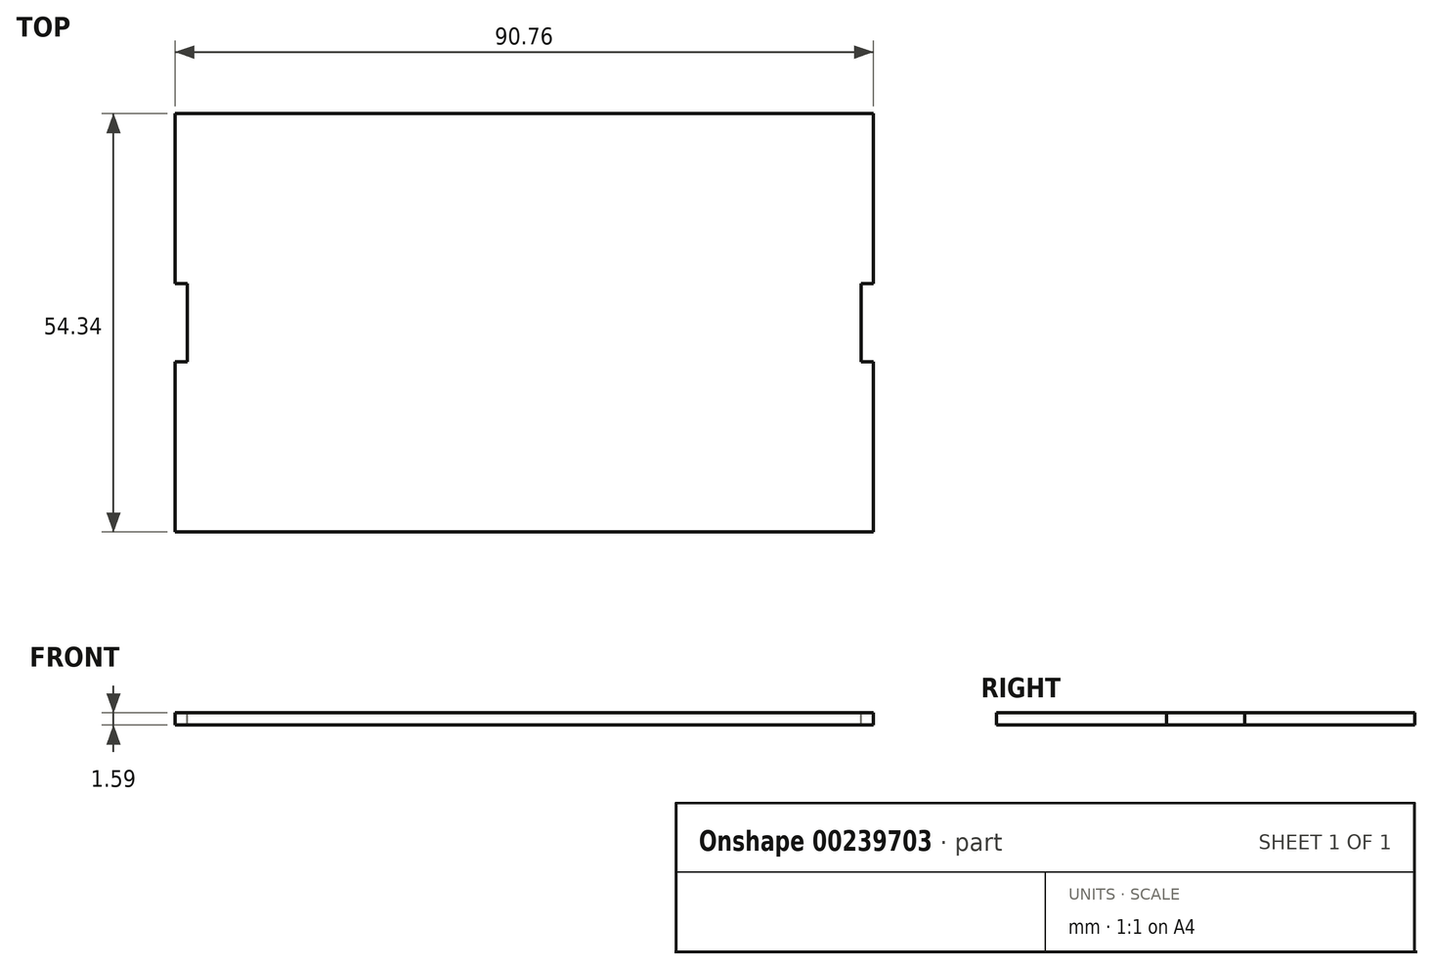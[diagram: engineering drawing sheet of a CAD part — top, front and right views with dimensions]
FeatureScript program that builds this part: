
annotation { "Feature Type Name" : "Feature", "Feature Type Description" : "" }
export const myFeature = defineFeature(function(context is Context, id is Id, definition is map)
    precondition{}
    {
        {
            var Q0;
            Q0=qCreatedBy(makeId("Top.planeOp"),FACE);
            var sketch = newSketch(context, id + "F0", { "sketchPlane" : qUnion([Q0])});
            skLineSegment(sketch, "E0.bottom", {"start": v(0, 0) * mm, "end": v(-90.76, 0) * mm});
            skLineSegment(sketch, "E0.top", {"start": v(0, 54.34) * mm, "end": v(-90.76, 54.34) * mm});
            skLineSegment(sketch, "E0.left", {"start": v(0, 0) * mm, "end": v(0, 54.34) * mm});
            skLineSegment(sketch, "E0.right", {"start": v(-90.76, 0) * mm, "end": v(-90.76, 54.34) * mm});
            skSolve(sketch);
        }
        {
            var Q0;
            Q0=makeQuery(id+"F0.imprint","IMPRINT",FACE,{"disambiguationData":[TD([[makeQuery(id+"F0.imprint","IMPRINT",EDGE,{"derivedFrom":sQuery(id+"F0.wireOp",EDGE,"E0.bottom")}),-1.0]])]});
            extrude(context, id + "F1", {"entities" : qUnion([Q0]), "depth" : 1.59 * mm});
        }
        {
            var Q0;
            Q0=makeQuery(id+"F1.opExtrude","CAP_FACE",FACE,{"disambiguationData":[OSD([sQuery(id+"F0.wireOp",EDGE,"E0.bottom"),sQuery(id+"F0.wireOp",EDGE,"E0.top"),sQuery(id+"F0.wireOp",EDGE,"E0.left"),sQuery(id+"F0.wireOp",EDGE,"E0.right")])],"isStart":false});
            var sketch = newSketch(context, id + "F2", { "sketchPlane" : qUnion([Q0])});
            skSolve(sketch);
        }
        {
            var Q0;
            Q0=makeQuery(id+"F2.imprint","IMPRINT",FACE,{"disambiguationData":[TD([[makeQuery(id+"F2.imprint","IMPRINT",EDGE,{"derivedFrom":makeQuery(id+"F1.opExtrude","CAP_EDGE",EDGE,{"disambiguationData":[OSD([sQuery(id+"F0.wireOp",EDGE,"E0.bottom")])],"isStart":false})}),-1.0]])]});
            var sketch = newSketch(context, id + "F3", { "sketchPlane" : qUnion([Q0])});
            skLineSegment(sketch, "E1", {"start": v(-45.38, 54.34) * mm, "end": v(-45.38, 0) * mm, "construction": true});
            skLineSegment(sketch, "E2.bottom", {"start": v(-90.76, 32.25) * mm, "end": v(-89.17, 32.25) * mm});
            skLineSegment(sketch, "E2.top", {"start": v(-90.76, 22.1) * mm, "end": v(-89.17, 22.1) * mm});
            skLineSegment(sketch, "E2.left", {"start": v(-90.76, 32.25) * mm, "end": v(-90.76, 22.1) * mm});
            skLineSegment(sketch, "E2.right", {"start": v(-89.17, 32.25) * mm, "end": v(-89.17, 22.1) * mm});
            skLineSegment(sketch, "E3", {"start": v(-90.76, 27.17) * mm, "end": v(0, 27.17) * mm, "construction": true});
            skLineSegment(sketch, "E4.MirrorCS", {"start": v(-1.59, 32.25) * mm, "end": v(-1.59, 22.1) * mm});
            skLineSegment(sketch, "E5.MirrorCS", {"start": v(0, 32.25) * mm, "end": v(0, 22.1) * mm});
            skLineSegment(sketch, "E6.MirrorCS", {"start": v(0, 32.25) * mm, "end": v(-1.59, 32.25) * mm});
            skLineSegment(sketch, "E7.MirrorCS", {"start": v(0, 22.1) * mm, "end": v(-1.59, 22.1) * mm});
            skSolve(sketch);
        }
        {
            var Q0;
            Q0 = qSketchRegion(id + "F3", true);
            extrude(context, id + "F4", {"entities" : qUnion([Q0]), "operationType" : NewBodyOperationType.REMOVE, "endBound" : BoundingType.THROUGH_ALL, "oppositeDirection" : true, "depth" : 25.4 * mm});
        }
    });
